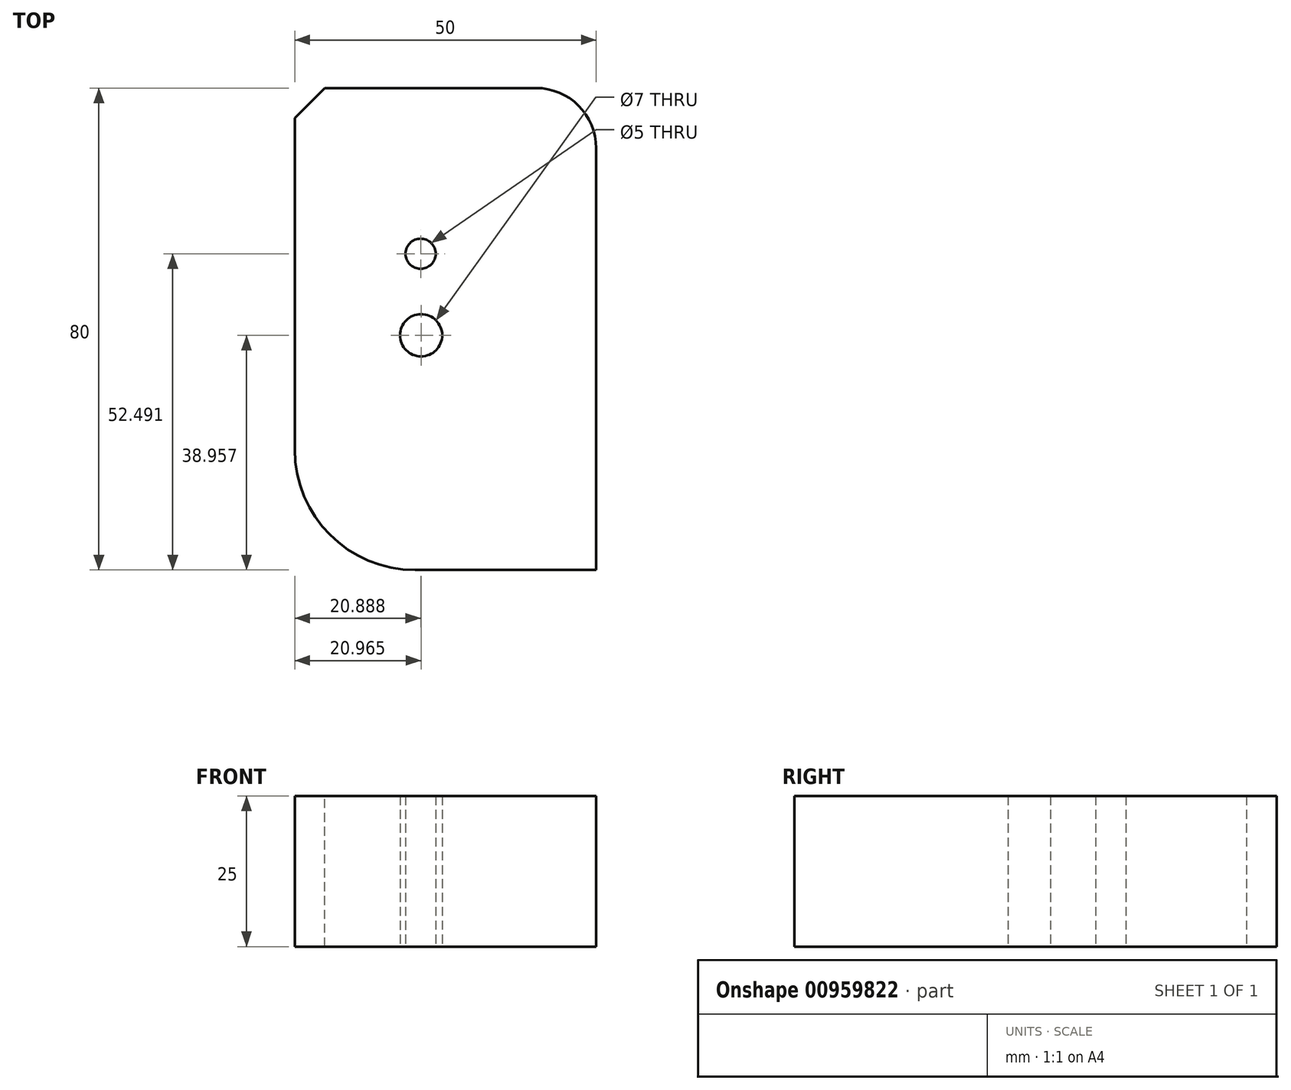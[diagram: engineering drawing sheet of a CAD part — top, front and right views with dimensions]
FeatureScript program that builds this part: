
annotation { "Feature Type Name" : "Feature", "Feature Type Description" : "" }
export const myFeature = defineFeature(function(context is Context, id is Id, definition is map)
    precondition{}
    {
        {
            var Q0;
            Q0=qCreatedBy(makeId("Top.planeOp"),FACE);
            var sketch = newSketch(context, id + "F0", { "sketchPlane" : qUnion([Q0])});
            skLineSegment(sketch, "E0.bottom", {"start": v(0, 0) * mm, "end": v(50, 0) * mm});
            skLineSegment(sketch, "E0.top", {"start": v(0, -80) * mm, "end": v(50, -80) * mm});
            skLineSegment(sketch, "E0.left", {"start": v(0, 0) * mm, "end": v(0, -80) * mm});
            skLineSegment(sketch, "E0.right", {"start": v(50, 0) * mm, "end": v(50, -80) * mm});
            skSolve(sketch);
        }
        {
            var Q0;
            Q0 = qSketchRegion(id + "F0", true);
            extrude(context, id + "F1", {"entities" : qUnion([Q0]), "depth" : 25 * mm, "offsetDistance" : 25 * mm});
        }
        {
            var Q0;
            Q0=makeQuery(id+"F1.opExtrude","SWEPT_EDGE",EDGE,{"disambiguationData":[OSD([sQuery(id+"F0.wireOp",EDGE,"E0.bottom"),sQuery(id+"F0.wireOp",EDGE,"E0.right")])]});
            fillet(context, id + "F2", {"entities" : qUnion([Q0]), "radius" : 10 * mm, "tangentPropagation" : true, "allowEdgeOverflow" : false});
        }
        {
            var Q0;
            Q0=makeQuery(id+"F1.opExtrude","SWEPT_EDGE",EDGE,{"disambiguationData":[OSD([sQuery(id+"F0.wireOp",EDGE,"E0.bottom"),sQuery(id+"F0.wireOp",EDGE,"E0.left")])]});
            chamfer(context, id + "F3", {"entities" : qUnion([Q0]), "width" : 5 * mm, "tangentPropagation" : true});
        }
        {
            var Q0;
            Q0=makeQuery(id+"F1.opExtrude","SWEPT_EDGE",EDGE,{"disambiguationData":[OSD([sQuery(id+"F0.wireOp",EDGE,"E0.top"),sQuery(id+"F0.wireOp",EDGE,"E0.left")])]});
            fillet(context, id + "F4", {"entities" : qUnion([Q0]), "radius" : 20 * mm, "tangentPropagation" : true, "allowEdgeOverflow" : false});
        }
        {
            var Q0;
            Q0=makeQuery(id+"F1.opExtrude","CAP_FACE",FACE,{"disambiguationData":[OSD([sQuery(id+"F0.wireOp",EDGE,"E0.bottom"),sQuery(id+"F0.wireOp",EDGE,"E0.top"),sQuery(id+"F0.wireOp",EDGE,"E0.left"),sQuery(id+"F0.wireOp",EDGE,"E0.right")])],"isStart":true});
            var sketch = newSketch(context, id + "F5", { "sketchPlane" : qUnion([Q0])});
            skCircle(sketch, "E1", {"center": v(20.89, 27.5) * mm, "radius": 2.5 * mm});
            skCircle(sketch, "E2", {"center": v(20.97, 41.04) * mm, "radius": 3.5 * mm});
            skSolve(sketch);
        }
        {
            var Q0;
            Q0 = qSketchRegion(id + "F5", true);
            extrude(context, id + "F6", {"entities" : qUnion([Q0]), "operationType" : NewBodyOperationType.REMOVE, "oppositeDirection" : true, "depth" : 30 * mm, "offsetDistance" : 25 * mm});
        }
    });
